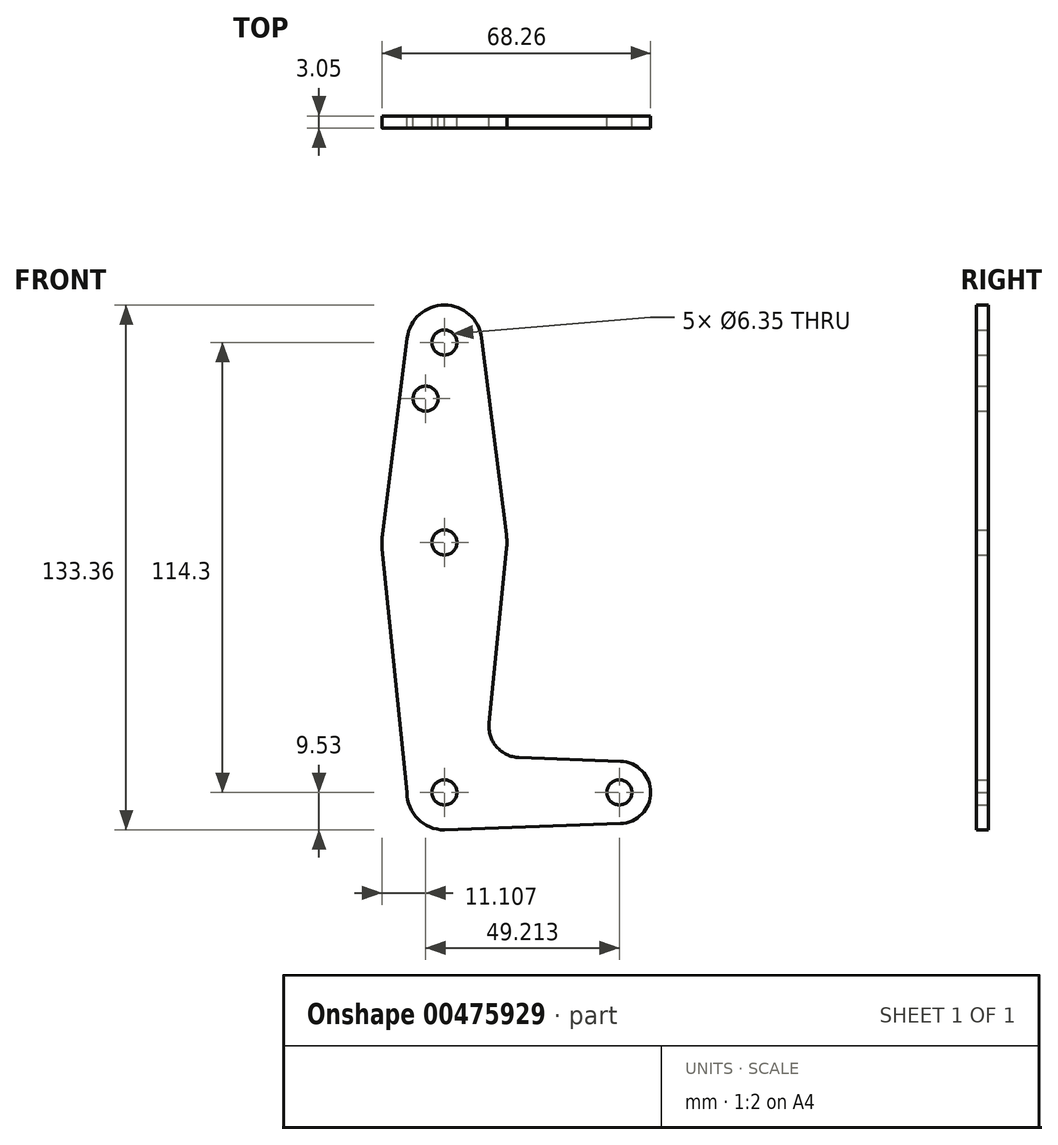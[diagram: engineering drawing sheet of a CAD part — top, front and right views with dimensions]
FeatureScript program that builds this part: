
annotation { "Feature Type Name" : "Feature", "Feature Type Description" : "" }
export const myFeature = defineFeature(function(context is Context, id is Id, definition is map)
    precondition{}
    {
        {
            var Q0;
            Q0=qCreatedBy(makeId("Front.planeOp"),FACE);
            var sketch = newSketch(context, id + "F0", { "sketchPlane" : qUnion([Q0])});
            skLineSegment(sketch, "E0", {"start": v(0, 0) * mm, "end": v(0, 114.3) * mm, "construction": true});
            skLineSegment(sketch, "E1", {"start": v(0, 0) * mm, "end": v(44.45, 0) * mm, "construction": true});
            skCircle(sketch, "E2", {"center": v(0, 0) * mm, "radius": 9.53 * mm});
            skCircle(sketch, "E3", {"center": v(44.45, 0) * mm, "radius": 7.94 * mm});
            skCircle(sketch, "E4", {"center": v(0, 63.5) * mm, "radius": 15.88 * mm});
            skCircle(sketch, "E5", {"center": v(0, 114.3) * mm, "radius": 9.53 * mm});
            skLineSegment(sketch, "E6", {"start": v(-9.45, 115.5) * mm, "end": v(-15.75, 65.48) * mm});
            skLineSegment(sketch, "E7", {"start": v(9.45, 115.5) * mm, "end": v(15.75, 65.48) * mm});
            skLineSegment(sketch, "E8", {"start": v(-9.52, 0) * mm, "end": v(-15.8, 61.9) * mm});
            skLineSegment(sketch, "E9", {"start": v(0, -9.53) * mm, "end": v(44.73, -7.93) * mm});
            skCircle(sketch, "E10", {"center": v(0, 114.3) * mm, "radius": 3.18 * mm});
            skCircle(sketch, "E11", {"center": v(0, 63.5) * mm, "radius": 3.18 * mm});
            skCircle(sketch, "E12", {"center": v(-4.76, 100.03) * mm, "radius": 3.18 * mm});
            skCircle(sketch, "E13", {"center": v(0, 0) * mm, "radius": 3.18 * mm});
            skCircle(sketch, "E14", {"center": v(44.45, 0) * mm, "radius": 3.18 * mm});
            skLineSegment(sketch, "E15", {"start": v(44.73, 7.93) * mm, "end": v(18.97, 8.85) * mm});
            skLineSegment(sketch, "E16", {"start": v(11.34, 17.6) * mm, "end": v(15.8, 61.91) * mm});
            skPoint(sketch, "E17.newPointA", {"position": v(0, 9.53) * mm});
            skArc(sketch, "E17.filletArc", {"start": v(11.34, 17.6) * mm, "mid": v(13.26, 11.57) * mm, "end": v(18.97, 8.85) * mm});
            skSolve(sketch);
        }
        {
            var Q0;
            Q0=makeQuery(id+"F0.imprint","IMPRINT",FACE,{"disambiguationData":[TD([[makeQuery(id+"F0.imprint","IMPRINT",EDGE,{"derivedFrom":sQuery(id+"F0.wireOp",EDGE,"E10")}),-1.0]])]});
            var Q1;
            {var subQ1=sQuery(id+"F0.wireOp",EDGE,"E6");Q1=makeQuery(id+"F0.imprint","IMPRINT",FACE,{"disambiguationData":[TD([[makeQuery(id+"F0.imprint","IMPRINT",EDGE,{"derivedFrom":subQ1}),1.0]])]});}
            var Q2;
            Q2=makeQuery(id+"F0.imprint","IMPRINT",FACE,{"disambiguationData":[TD([[makeQuery(id+"F0.imprint","IMPRINT",EDGE,{"derivedFrom":sQuery(id+"F0.wireOp",EDGE,"E11")}),-1.0]])]});
            var Q3;
            {var subQ0=sQuery(id+"F0.wireOp",EDGE,"E8");Q3=makeQuery(id+"F0.imprint","IMPRINT",FACE,{"disambiguationData":[TD([[makeQuery(id+"F0.imprint","IMPRINT",EDGE,{"derivedFrom":subQ0}),-1.0]])]});}
            var Q4;
            Q4=makeQuery(id+"F0.imprint","IMPRINT",FACE,{"disambiguationData":[TD([[makeQuery(id+"F0.imprint","IMPRINT",EDGE,{"derivedFrom":sQuery(id+"F0.wireOp",EDGE,"E13")}),-1.0]])]});
            var Q5;
            Q5=makeQuery(id+"F0.imprint","IMPRINT",FACE,{"disambiguationData":[TD([[makeQuery(id+"F0.imprint","IMPRINT",EDGE,{"derivedFrom":sQuery(id+"F0.wireOp",EDGE,"E14")}),-1.0]])]});
            var Q6;
            {var subQ0=sQuery(id+"F0.wireOp",EDGE,"E9");var subQ1=sQuery(id+"F0.wireOp",EDGE,"E2");var subQ2=makeQuery(id+"F0.imprint","INTERSECT",VERTEX,{"disambiguationData":[OD(0.0)],"derivedFrom":[subQ1,subQ0]});Q6=makeQuery(id+"F0.imprint","IMPRINT",FACE,{"disambiguationData":[TD([[makeQuery(id+"F0.imprint","IMPRINT",EDGE,{"disambiguationData":[TD([[subQ2,-1.0]])],"derivedFrom":subQ1}),1.0]])]});}
            extrude(context, id + "F1", {"entities" : qUnion([Q0, Q1, Q2, Q3, Q4, Q5, Q6]), "depth" : 3.05 * mm});
        }
    });
